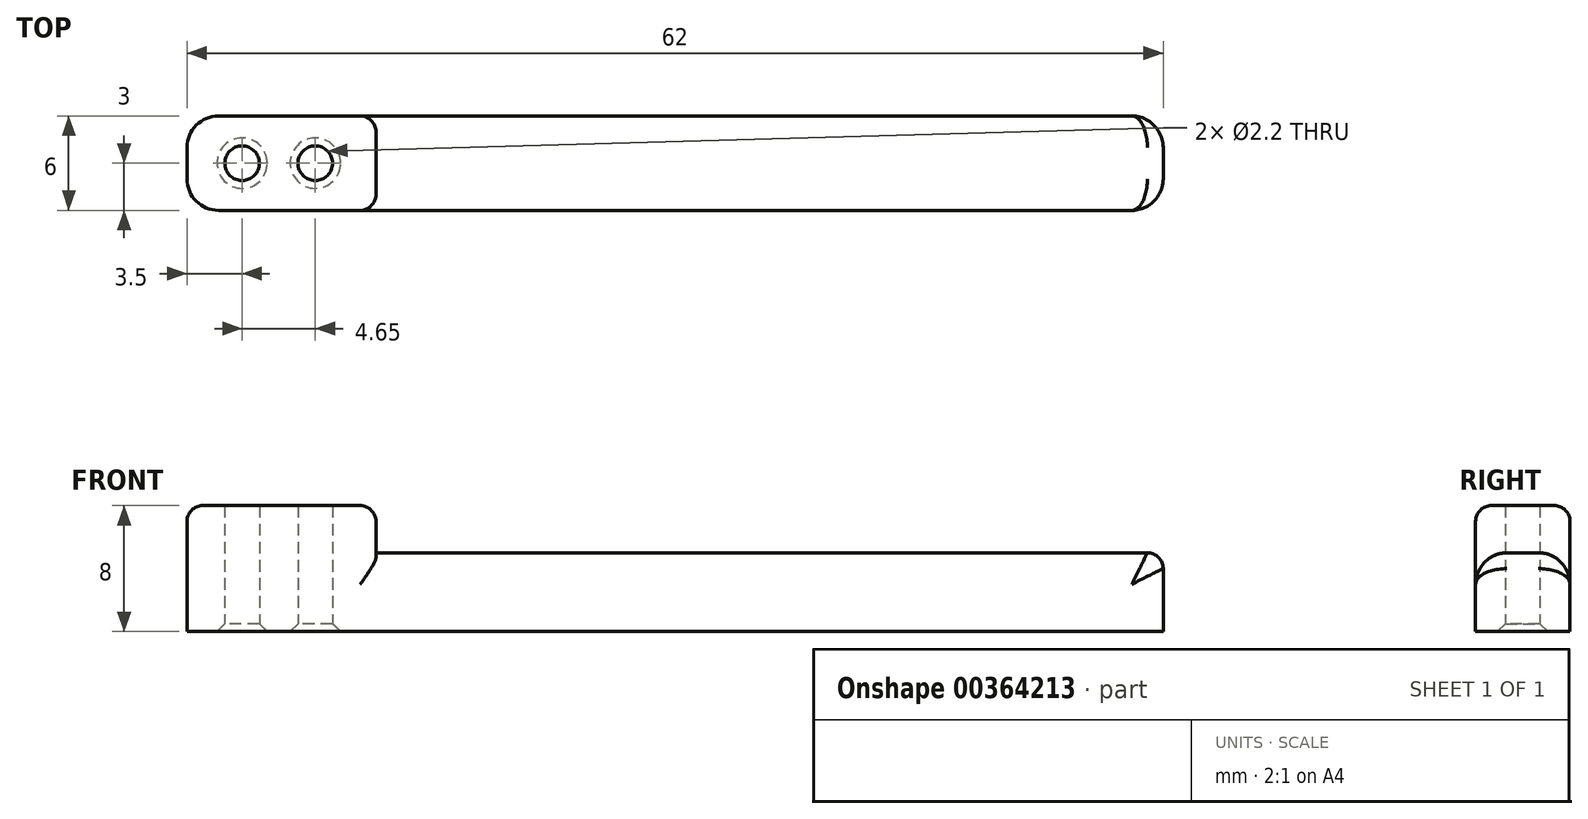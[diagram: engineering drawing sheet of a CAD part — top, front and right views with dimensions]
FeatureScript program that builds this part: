
annotation { "Feature Type Name" : "Feature", "Feature Type Description" : "" }
export const myFeature = defineFeature(function(context is Context, id is Id, definition is map)
    precondition{}
    {
        {
            var Q0;
            Q0=qCreatedBy(makeId("Top.planeOp"),FACE);
            var sketch = newSketch(context, id + "F0", { "sketchPlane" : qUnion([Q0])});
            skPoint(sketch, "E0.middle", {"position": v(0, 0) * mm});
            skCircle(sketch, "E1", {"center": v(-2.5, 0) * mm, "radius": 1.1 * mm});
            skCircle(sketch, "E2", {"center": v(2.15, 0) * mm, "radius": 1.1 * mm});
            skPoint(sketch, "E0.right.end.orphan", {"position": v(-4.81, 2.23) * mm});
            skPoint(sketch, "E0.bottom.end.orphan", {"position": v(-4.81, -2.23) * mm});
            skPoint(sketch, "E0.left.end.orphan", {"position": v(4.81, 2.23) * mm});
            skPoint(sketch, "E0.left.start.orphan", {"position": v(4.81, -2.23) * mm});
            skLineSegment(sketch, "E3.bottom", {"start": v(6, -3) * mm, "end": v(-6, -3) * mm});
            skLineSegment(sketch, "E3.top", {"start": v(6, 3) * mm, "end": v(-6, 3) * mm});
            skLineSegment(sketch, "E3.right", {"start": v(-6, -3) * mm, "end": v(-6, 3) * mm});
            skLineSegment(sketch, "E4", {"start": v(0, 0) * mm, "end": v(3.25, 0) * mm});
            skLineSegment(sketch, "E5", {"start": v(6, 3) * mm, "end": v(6, -3) * mm});
            skSolve(sketch);
        }
        {
            var Q0;
            Q0 = qSketchRegion(id + "F0", true);
            extrude(context, id + "F1", {"entities" : qUnion([Q0]), "depth" : 8 * mm});
        }
        {
            var Q0;
            Q0=qCreatedBy(makeId("Top.planeOp"),FACE);
            var sketch = newSketch(context, id + "F2", { "sketchPlane" : qUnion([Q0])});
            skLineSegment(sketch, "E6", {"start": v(0, 0) * mm, "end": v(6, 0) * mm});
            skLineSegment(sketch, "E7", {"start": v(56, 0) * mm, "end": v(56, 3) * mm});
            skLineSegment(sketch, "E8", {"start": v(56, 3) * mm, "end": v(6, 3) * mm});
            skLineSegment(sketch, "E9", {"start": v(6, 3) * mm, "end": v(6, -3) * mm});
            skLineSegment(sketch, "E10", {"start": v(6, -3) * mm, "end": v(56, -3) * mm});
            skLineSegment(sketch, "E11", {"start": v(56, -3) * mm, "end": v(56, 0) * mm});
            skSolve(sketch);
        }
        {
            var Q0;
            Q0 = qSketchRegion(id + "F2", true);
            extrude(context, id + "F3", {"entities" : qUnion([Q0]), "operationType" : NewBodyOperationType.ADD, "depth" : 5 * mm});
        }
        {
            var Q0;
            Q0=makeQuery(id+"F1.opExtrude","CAP_EDGE",EDGE,{"disambiguationData":[OSD([sQuery(id+"F0.wireOp",EDGE,"E1")])],"isStart":true});
            var Q1;
            Q1=makeQuery(id+"F1.opExtrude","CAP_EDGE",EDGE,{"disambiguationData":[OSD([sQuery(id+"F0.wireOp",EDGE,"E2")])],"isStart":true});
            chamfer(context, id + "F4", {"entities" : qUnion([Q0, Q1]), "width" : 0.5 * mm, "tangentPropagation" : true});
        }
        {
            var Q0;
            Q0=makeQuery(id+"F3.opExtrude","CAP_EDGE",EDGE,{"disambiguationData":[OSD([sQuery(id+"F2.wireOp",EDGE,"E9")])],"isStart":false});
            var Q1;
            Q1=makeQuery(id+"F1.opExtrude","SWEPT_EDGE",EDGE,{"disambiguationData":[OSD([sQuery(id+"F0.wireOp",EDGE,"E3.bottom"),sQuery(id+"F0.wireOp",EDGE,"E5")])]});
            var Q2;
            Q2=makeQuery(id+"F1.opExtrude","SWEPT_EDGE",EDGE,{"disambiguationData":[OSD([sQuery(id+"F0.wireOp",EDGE,"E3.top"),sQuery(id+"F0.wireOp",EDGE,"E5")])]});
            var Q3;
            Q3=makeQuery(id+"F3.opExtrude","CAP_EDGE",EDGE,{"disambiguationData":[OSD([sQuery(id+"F2.wireOp",EDGE,"E7"),sQuery(id+"F2.wireOp",EDGE,"E11")])],"isStart":false});
            var Q4;
            Q4=makeQuery(id+"F1.opExtrude","CAP_EDGE",EDGE,{"disambiguationData":[OSD([sQuery(id+"F0.wireOp",EDGE,"E3.bottom")])],"isStart":false});
            var Q5;
            Q5=makeQuery(id+"F1.opExtrude","CAP_EDGE",EDGE,{"disambiguationData":[OSD([sQuery(id+"F0.wireOp",EDGE,"E5")])],"isStart":false});
            var Q6;
            Q6=makeQuery(id+"F1.opExtrude","CAP_EDGE",EDGE,{"disambiguationData":[OSD([sQuery(id+"F0.wireOp",EDGE,"E3.top")])],"isStart":false});
            var Q7;
            Q7=makeQuery(id+"F1.opExtrude","CAP_EDGE",EDGE,{"disambiguationData":[OSD([sQuery(id+"F0.wireOp",EDGE,"E3.right")])],"isStart":false});
            fillet(context, id + "F5", {"entities" : qUnion([Q0, Q1, Q2, Q3, Q4, Q5, Q6, Q7]), "radius" : 1 * mm, "tangentPropagation" : true, "allowEdgeOverflow" : false});
        }
        {
            var Q0;
            Q0=makeQuery(id+"F1.opExtrude","SWEPT_EDGE",EDGE,{"disambiguationData":[OSD([sQuery(id+"F0.wireOp",EDGE,"E3.bottom"),sQuery(id+"F0.wireOp",EDGE,"E3.right")])]});
            var Q1;
            Q1=makeQuery(id+"F1.opExtrude","SWEPT_EDGE",EDGE,{"disambiguationData":[OSD([sQuery(id+"F0.wireOp",EDGE,"E3.top"),sQuery(id+"F0.wireOp",EDGE,"E3.right")])]});
            var Q2;
            Q2=makeQuery(id+"F3.opExtrude","SWEPT_EDGE",EDGE,{"disambiguationData":[OSD([sQuery(id+"F2.wireOp",EDGE,"E10"),sQuery(id+"F2.wireOp",EDGE,"E11")])]});
            var Q3;
            Q3=makeQuery(id+"F3.opExtrude","SWEPT_EDGE",EDGE,{"disambiguationData":[OSD([sQuery(id+"F2.wireOp",EDGE,"E7"),sQuery(id+"F2.wireOp",EDGE,"E8")])]});
            fillet(context, id + "F6", {"entities" : qUnion([Q0, Q1, Q2, Q3]), "radius" : 2 * mm, "tangentPropagation" : true, "allowEdgeOverflow" : false});
        }
    });
